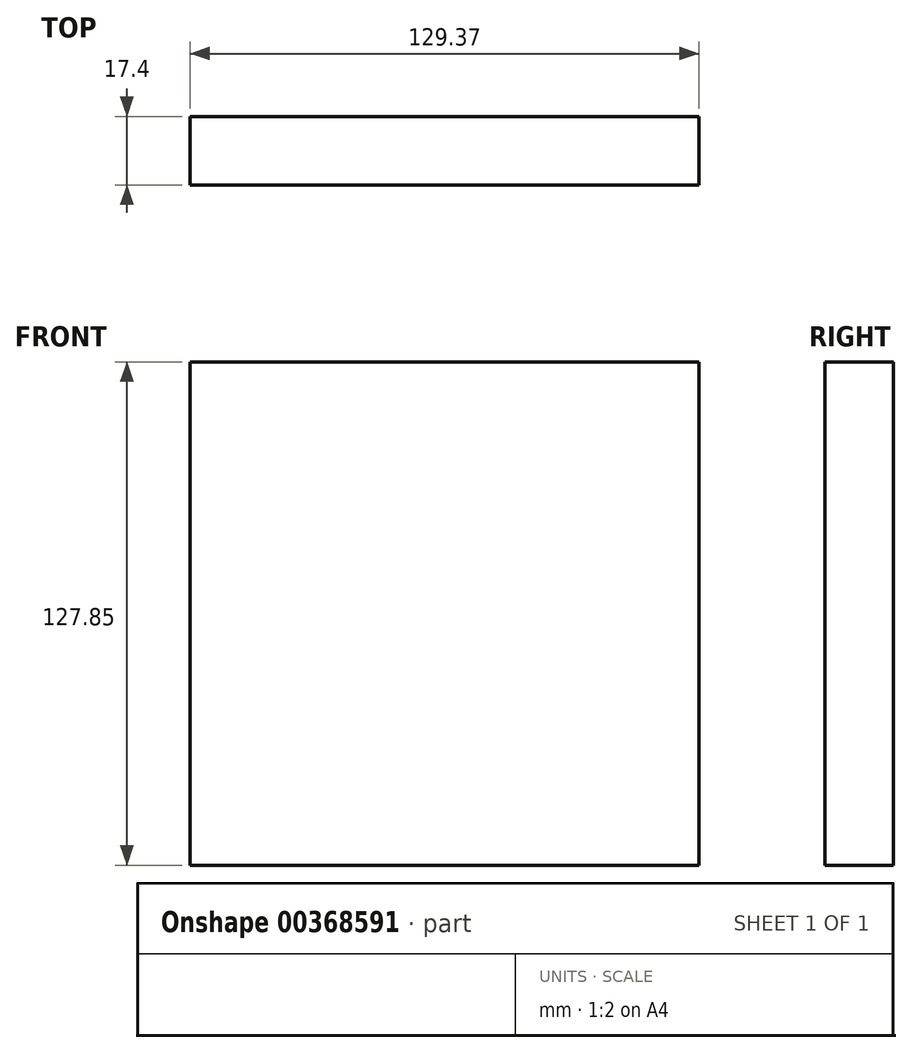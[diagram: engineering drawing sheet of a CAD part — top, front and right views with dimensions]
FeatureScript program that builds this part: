
annotation { "Feature Type Name" : "Feature", "Feature Type Description" : "" }
export const myFeature = defineFeature(function(context is Context, id is Id, definition is map)
    precondition{}
    {
        {
            var Q0;
            Q0=qCreatedBy(makeId("Front.planeOp"),FACE);
            var sketch = newSketch(context, id + "F0", { "sketchPlane" : qUnion([Q0])});
            skLineSegment(sketch, "E0", {"start": v(-58.8, 66.54) * mm, "end": v(70.57, 66.54) * mm});
            skLineSegment(sketch, "E1", {"start": v(70.57, 66.54) * mm, "end": v(70.57, -61.3) * mm});
            skLineSegment(sketch, "E2", {"start": v(-58.8, -61.3) * mm, "end": v(70.57, -61.3) * mm});
            skLineSegment(sketch, "E3", {"start": v(-58.8, -61.3) * mm, "end": v(-58.8, 66.54) * mm});
            skSolve(sketch);
        }
        {
            var Q0;
            Q0=makeQuery(id+"F0.imprint","IMPRINT",FACE,{"disambiguationData":[TD([[makeQuery(id+"F0.imprint","IMPRINT",EDGE,{"derivedFrom":sQuery(id+"F0.wireOp",EDGE,"E0")}),-1.0]])]});
            extrude(context, id + "F1", {"entities" : qUnion([Q0]), "depth" : 17.4 * mm});
        }
    });
